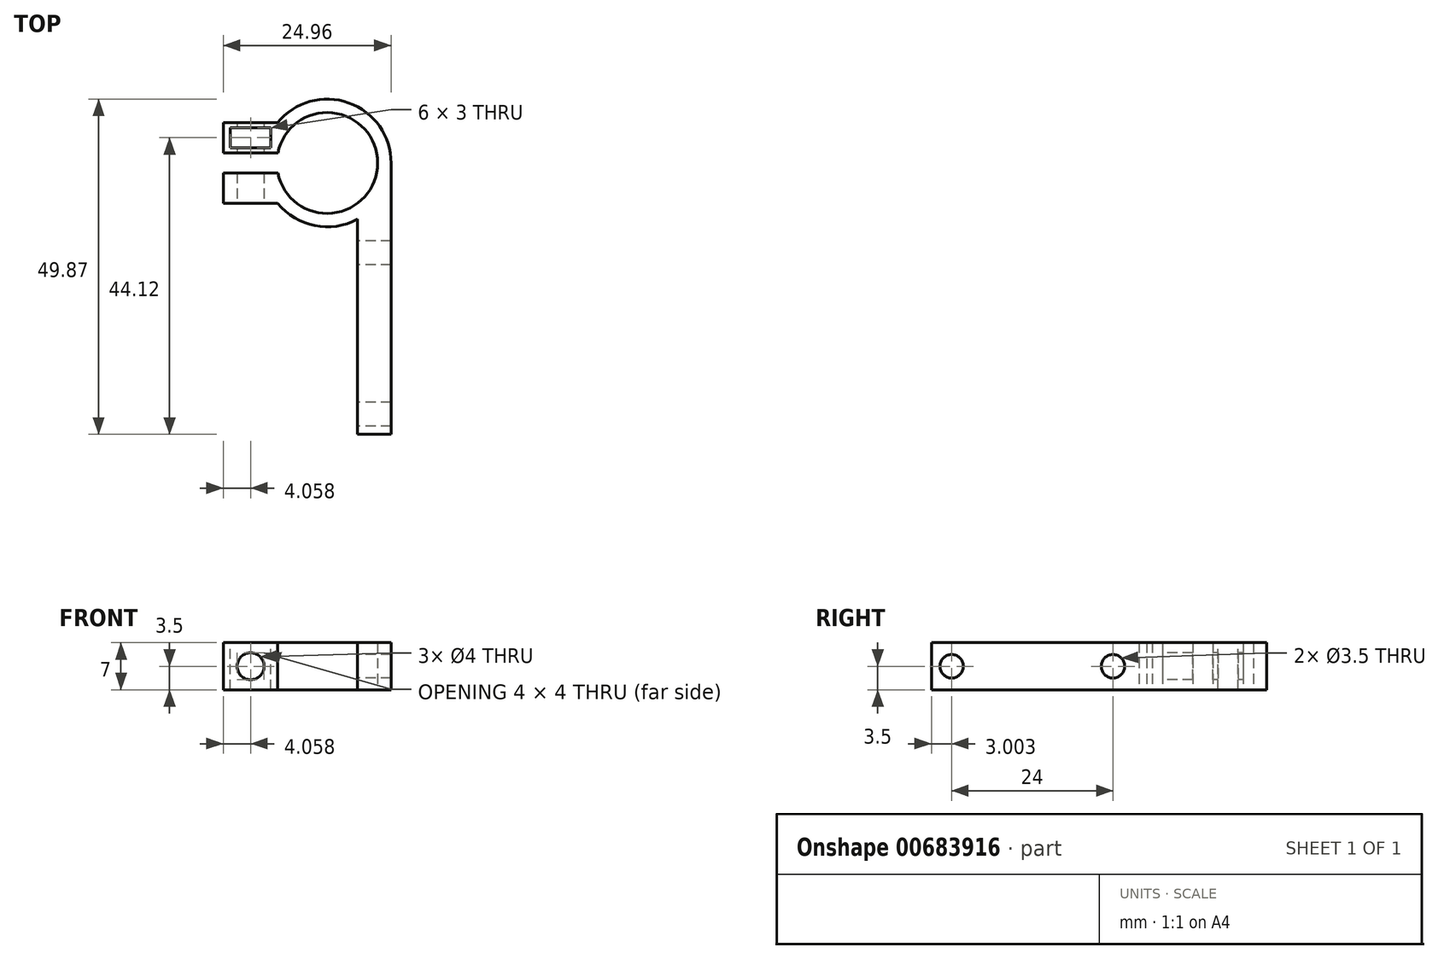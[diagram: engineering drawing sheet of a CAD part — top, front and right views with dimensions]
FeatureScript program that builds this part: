
annotation { "Feature Type Name" : "Feature", "Feature Type Description" : "" }
export const myFeature = defineFeature(function(context is Context, id is Id, definition is map)
    precondition{}
    {
        {
            var Q0;
            Q0=qCreatedBy(makeId("Top.planeOp"),FACE);
            var sketch = newSketch(context, id + "F0", { "sketchPlane" : qUnion([Q0])});
            skCircle(sketch, "E0", {"center": v(0, 0) * mm, "radius": 7.5 * mm});
            skLineSegment(sketch, "E1", {"start": v(-15.46, 0) * mm, "end": v(-15.46, -6) * mm});
            skLineSegment(sketch, "E2", {"start": v(-15.46, -6) * mm, "end": v(-7.37, -6) * mm});
            skLineSegment(sketch, "E3", {"start": v(-15.46, 0) * mm, "end": v(-7.5, 0) * mm});
            skLineSegment(sketch, "E4", {"start": v(-15.46, 0) * mm, "end": v(-15.46, 6) * mm});
            skLineSegment(sketch, "E5", {"start": v(-15.46, 6) * mm, "end": v(-4.5, 6) * mm});
            skLineSegment(sketch, "E6.bottom", {"start": v(-7.35, 1.5) * mm, "end": v(-15.6, 1.5) * mm});
            skLineSegment(sketch, "E6.top", {"start": v(-7.35, -1.5) * mm, "end": v(-15.6, -1.5) * mm});
            skLineSegment(sketch, "E6.left", {"start": v(-7.35, 1.5) * mm, "end": v(-7.35, -1.5) * mm});
            skLineSegment(sketch, "E6.right", {"start": v(-15.6, 1.5) * mm, "end": v(-15.6, -1.5) * mm});
            skPoint(sketch, "E6.middle", {"position": v(-11.48, 0) * mm});
            skLineSegment(sketch, "E7", {"start": v(9.5, 0) * mm, "end": v(9.5, -40.37) * mm});
            skLineSegment(sketch, "E8", {"start": v(4.5, -40.37) * mm, "end": v(4.5, -8.37) * mm});
            skLineSegment(sketch, "E9", {"start": v(9.5, -40.37) * mm, "end": v(4.5, -40.37) * mm});
            skCircle(sketch, "E10", {"center": v(0, 0) * mm, "radius": 9.5 * mm});
            skSolve(sketch);
        }
        {
            var Q0;
            {var subQ0=sQuery(id+"F0.wireOp",EDGE,"G5YJE7GE-uxO1-jhGu-FKWH-EMHxi7iK1pYa");var subQ1=makeQuery(id+"F0.imprint","INTERSECT",VERTEX,{"derivedFrom":[subQ0,sQuery(id+"F0.wireOp",EDGE,"5D6cqXOa-psys-zM7H-t359-fMBPCfmSysQQ")]});Q0=makeQuery(id+"F0.imprint","IMPRINT",FACE,{"disambiguationData":[TD([[makeQuery(id+"F0.imprint","IMPRINT",EDGE,{"disambiguationData":[TD([[subQ1,1.0]])],"derivedFrom":subQ0}),1.0]])]});}
            var Q1;
            {var subQ0=sQuery(id+"F0.wireOp",EDGE,"E2");Q1=makeQuery(id+"F0.imprint","IMPRINT",FACE,{"disambiguationData":[TD([[makeQuery(id+"F0.imprint","IMPRINT",EDGE,{"derivedFrom":subQ0}),1.0]])]});}
            var Q2;
            {var subQ0=sQuery(id+"F0.wireOp",EDGE,"E5");var subQ5=sQuery(id+"F0.wireOp",EDGE,"G5YJE7GE-uxO1-jhGu-FKWH-EMHxi7iK1pYa");var subQ7=makeQuery(id+"F0.imprint","INTERSECT",VERTEX,{"derivedFrom":[subQ5,subQ0]});Q2=makeQuery(id+"F0.imprint","IMPRINT",FACE,{"disambiguationData":[TD([[makeQuery(id+"F0.imprint","IMPRINT",EDGE,{"disambiguationData":[TD([[subQ7,-1.0]])],"derivedFrom":subQ5}),1.0]])]});}
            var Q3;
            {var subQ0=sQuery(id+"F0.wireOp",EDGE,"E5");var subQ1=sQuery(id+"F0.wireOp",EDGE,"G5YJE7GE-uxO1-jhGu-FKWH-EMHxi7iK1pYa");var subQ2=makeQuery(id+"F0.imprint","INTERSECT",VERTEX,{"derivedFrom":[subQ1,subQ0]});Q3=makeQuery(id+"F0.imprint","IMPRINT",FACE,{"disambiguationData":[TD([[makeQuery(id+"F0.imprint","IMPRINT",EDGE,{"disambiguationData":[TD([[subQ2,-1.0]])],"derivedFrom":subQ1}),-1.0]])]});}
            var Q4;
            {var subQ2=sQuery(id+"F0.wireOp",EDGE,"E5");var subQ4=sQuery(id+"F0.wireOp",EDGE,"E0");var subQ5=makeQuery(id+"F0.imprint","INTERSECT",VERTEX,{"derivedFrom":[subQ4,subQ2]});Q4=makeQuery(id+"F0.imprint","IMPRINT",FACE,{"disambiguationData":[TD([[makeQuery(id+"F0.imprint","IMPRINT",EDGE,{"disambiguationData":[TD([[subQ5,1.0]])],"derivedFrom":subQ2}),1.0]])]});}
            var Q5;
            {var subQ0=sQuery(id+"F0.wireOp",EDGE,"E5");var subQ1=sQuery(id+"F0.wireOp",EDGE,"E0");var subQ2=makeQuery(id+"F0.imprint","INTERSECT",VERTEX,{"derivedFrom":[subQ1,subQ0]});Q5=makeQuery(id+"F0.imprint","IMPRINT",FACE,{"disambiguationData":[TD([[makeQuery(id+"F0.imprint","IMPRINT",EDGE,{"disambiguationData":[TD([[subQ2,1.0]])],"derivedFrom":subQ0}),-1.0]])]});}
            var Q6;
            {var subQ0=sQuery(id+"F0.wireOp",EDGE,"E5");var subQ1=sQuery(id+"F0.wireOp",EDGE,"E4");var subQ2=makeQuery(id+"F0.imprint","INTERSECT",VERTEX,{"derivedFrom":[subQ1,subQ0]});Q6=makeQuery(id+"F0.imprint","IMPRINT",FACE,{"disambiguationData":[TD([[makeQuery(id+"F0.imprint","IMPRINT",EDGE,{"disambiguationData":[TD([[subQ2,1.0]])],"derivedFrom":subQ1}),-1.0]])]});}
            var Q7;
            {var subQ4=sQuery(id+"F0.wireOp",EDGE,"E8");Q7=makeQuery(id+"F0.imprint","IMPRINT",FACE,{"disambiguationData":[TD([[makeQuery(id+"F0.imprint","IMPRINT",EDGE,{"derivedFrom":subQ4}),-1.0]])]});}
            extrude(context, id + "F1", {"entities" : qUnion([Q0, Q1, Q2, Q3, Q4, Q5, Q6, Q7]), "depth" : 7 * mm, "offsetDistance" : 25 * mm});
        }
        {
            var Q0;
            Q0=makeQuery(id+"F1.opExtrude","CAP_FACE",FACE,{"disambiguationData":[OSD([sQuery(id+"F0.wireOp",EDGE,"E0"),sQuery(id+"F0.wireOp",EDGE,"G5YJE7GE-uxO1-jhGu-FKWH-EMHxi7iK1pYa"),sQuery(id+"F0.wireOp",EDGE,"E1"),sQuery(id+"F0.wireOp",EDGE,"E2"),sQuery(id+"F0.wireOp",EDGE,"E4"),sQuery(id+"F0.wireOp",EDGE,"E5"),sQuery(id+"F0.wireOp",EDGE,"E6.bottom"),sQuery(id+"F0.wireOp",EDGE,"E6.top"),sQuery(id+"F0.wireOp",EDGE,"E7"),sQuery(id+"F0.wireOp",EDGE,"E8"),sQuery(id+"F0.wireOp",EDGE,"E9")])],"isStart":false});
            var sketch = newSketch(context, id + "F2", { "sketchPlane" : qUnion([Q0])});
            skLineSegment(sketch, "E11", {"start": v(-15.46, 3.75) * mm, "end": v(-11.4, 3.75) * mm, "construction": true});
            skLineSegment(sketch, "E12", {"start": v(-11.4, 3.75) * mm, "end": v(-11.4, 1.5) * mm, "construction": true});
            skLineSegment(sketch, "E13.bottom", {"start": v(-8.4, 5.25) * mm, "end": v(-14.4, 5.25) * mm});
            skLineSegment(sketch, "E13.top", {"start": v(-8.4, 2.25) * mm, "end": v(-14.4, 2.25) * mm});
            skLineSegment(sketch, "E13.left", {"start": v(-8.4, 5.25) * mm, "end": v(-8.4, 2.25) * mm});
            skLineSegment(sketch, "E13.right", {"start": v(-14.4, 5.25) * mm, "end": v(-14.4, 2.25) * mm});
            skPoint(sketch, "E13.middle", {"position": v(-11.4, 3.75) * mm});
            skSolve(sketch);
        }
        {
            var Q0;
            Q0=makeQuery(id+"F2.imprint","IMPRINT",FACE,{"disambiguationData":[TD([[makeQuery(id+"F2.imprint","IMPRINT",EDGE,{"derivedFrom":sQuery(id+"F2.wireOp",EDGE,"E13.bottom")}),1.0]])]});
            extrude(context, id + "F3", {"entities" : qUnion([Q0]), "operationType" : NewBodyOperationType.REMOVE, "endBound" : BoundingType.THROUGH_ALL, "oppositeDirection" : true, "depth" : 25 * mm, "offsetDistance" : 25 * mm});
        }
        {
            var Q0;
            Q0=makeQuery(id+"F1.opExtrude","SWEPT_FACE",FACE,{"disambiguationData":[OSD([sQuery(id+"F0.wireOp",EDGE,"E8")])]});
            var sketch = newSketch(context, id + "F4", { "sketchPlane" : qUnion([Q0])});
            skLineSegment(sketch, "E14", {"start": v(40.37, 3.5) * mm, "end": v(37.37, 3.5) * mm, "construction": true});
            skLineSegment(sketch, "E15", {"start": v(37.37, 3.5) * mm, "end": v(13.37, 3.5) * mm, "construction": true});
            skCircle(sketch, "E16", {"center": v(13.37, 3.5) * mm, "radius": 1.75 * mm});
            skCircle(sketch, "E17", {"center": v(37.37, 3.5) * mm, "radius": 1.75 * mm});
            skSolve(sketch);
        }
        {
            var Q0;
            Q0=makeQuery(id+"F4.imprint","IMPRINT",FACE,{"disambiguationData":[TD([[makeQuery(id+"F4.imprint","IMPRINT",EDGE,{"derivedFrom":sQuery(id+"F4.wireOp",EDGE,"E16")}),1.0]])]});
            var Q1;
            Q1=makeQuery(id+"F4.imprint","IMPRINT",FACE,{"disambiguationData":[TD([[makeQuery(id+"F4.imprint","IMPRINT",EDGE,{"derivedFrom":sQuery(id+"F4.wireOp",EDGE,"E17")}),1.0]])]});
            extrude(context, id + "F5", {"entities" : qUnion([Q0, Q1]), "operationType" : NewBodyOperationType.REMOVE, "endBound" : BoundingType.THROUGH_ALL, "oppositeDirection" : true, "depth" : 25 * mm, "offsetDistance" : 25 * mm});
        }
        {
            var Q0;
            Q0=makeQuery(id+"F3.boolean.opBoolean","COPY",FACE,{"derivedFrom":makeQuery(id+"F3.opExtrude","SWEPT_FACE",FACE,{"disambiguationData":[OSD([sQuery(id+"F2.wireOp",EDGE,"E13.bottom")])]})});
            var sketch = newSketch(context, id + "F6", { "sketchPlane" : qUnion([Q0])});
            skLineSegment(sketch, "E18", {"start": v(-11.4, 7) * mm, "end": v(-11.4, 3.5) * mm, "construction": true});
            skLineSegment(sketch, "E19", {"start": v(-11.4, 3.5) * mm, "end": v(-14.4, 3.5) * mm, "construction": true});
            skCircle(sketch, "E20", {"center": v(-11.4, 3.5) * mm, "radius": 2 * mm});
            skSolve(sketch);
        }
        {
            var Q0;
            Q0=makeQuery(id+"F6.imprint","IMPRINT",FACE,{"disambiguationData":[TD([[makeQuery(id+"F6.imprint","IMPRINT",EDGE,{"derivedFrom":sQuery(id+"F6.wireOp",EDGE,"E20")}),1.0]])]});
            extrude(context, id + "F7", {"entities" : qUnion([Q0]), "operationType" : NewBodyOperationType.REMOVE, "endBound" : BoundingType.THROUGH_ALL, "oppositeDirection" : true, "depth" : 25 * mm, "offsetDistance" : 25 * mm, "hasSecondDirection" : true, "secondDirectionBound" : SecondDirectionBoundingType.THROUGH_ALL, "secondDirectionOppositeDirection" : false, "secondDirectionDepth" : 25 * mm});
        }
    });
